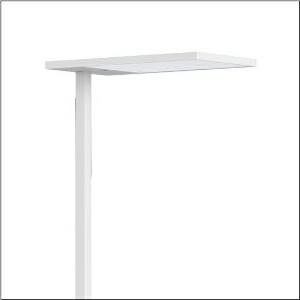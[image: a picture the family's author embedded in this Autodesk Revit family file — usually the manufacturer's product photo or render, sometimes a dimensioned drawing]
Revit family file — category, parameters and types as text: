
# Revit family: silica_r__21_floor_r_51mx53sg4dw_45fa
name_source: partatom
category: Lighting Fixtures
units: mm (PartAtom-declared; Revit-internal decimal feet)

## family parameters
Cut with Voids When Loaded = No
Host = Face
Light Source = No
Part Type = Normal
Room Calculation Point = No
Round Connector Dimension = Use Diameter
Shared = No

## types (1)
- Silica® 21 Floor R (1 x LED, 15000 lm, 106.4 W, 4000K)
    Apparent Load = 106 VA
    CIE Flux Codes = 54 86 97 13 100
    Color Rendering = 80
    Color Temperature = 4000K
    Default Elevation = 1800 mm
    Description = Silica® 21 Floor R, floorstanding luminaire, of PMMA, primary optical cover: prismatic diffuser, of PMMA, CAT 2 (L<= 3000cd/m²), light emission: indirect/direct distribution, primary light characteristic: symmetric, primary optical cover: cover panel, of PMMA, installation type: not mounted, LED, rated luminous flux: 15.000lm, luminous efficacy: 141lm/W, light colour: 840, colour temperature: 4000K, control gear: DALI 2, daylight-dependent control, mains connection: 230V, AC, 50/60Hz, connection cable included, cable length: 2,5m, rated input power: 106.4W, luminaire head, of aluminium, powder-coated, traffic white (RAL 9016), length: 671mm, width: 371mm, height: 2010mm, supporting column, angular, of aluminium, powder-coated, traffic white (RAL 9016), baseplate, of steel, powder-coated, traffic white (RAL 9016), sensor module PR3-S, local control - self-sufficient standalone sensors, equipment: master, dimmable, protection rating (complete): IP20, insulation class (complete): insulation class I (protective earthing), certification: CE, standard: EN 50419, packaging unit: 1 piece
    Height = 18 mm
    Lamp = 1 x LED
    Lamp Light Flux = 15000 lm
    Lamp Power = 106.4 W
    Lamp count = 1
    Length = 650 mm
    Luminous efficacy = 141 lm/W
    Manufacturer = Siteco
    ModVariant = No
    Model = 51MX53SG4DW
    Mounting Place = Floor
    Mounting Type = Freestanding
    Number of Poles = 1
    OnlyDefault = Yes
    Power Factor = 1
    Product Name = Silica® 21 Floor R
    Product group = floorstanding luminaire
    ProductGroupID = 1302
    Protection Class = Protection class I
    Protection Degree = IP 20
    RLX_Detail_Level = 1
    RLX_Emergency_Light_Flux = 0 lm
    RLX_Emergency_Type = 0
    RLX_Emergency_Type_DB = No
    RlxData = <blob elided: 18873 chars, md5=be8b3077>
    Socket = socket
    Standby Power = 0 W
    System Light Flux = 15000 lm
    System Power = 106 W
    Type Comments = Product without accessories
    Type Image = l_1003935.jpg
    URL = http://relux.com
    VarID = ---
    Voltage = 0 V
    Weight = 0.00 kg
    Width = 350 mm

## geometry (parser evidence)
native form markers: Blend x4, Sweep x15
no freeform markers — native parametric forms only
